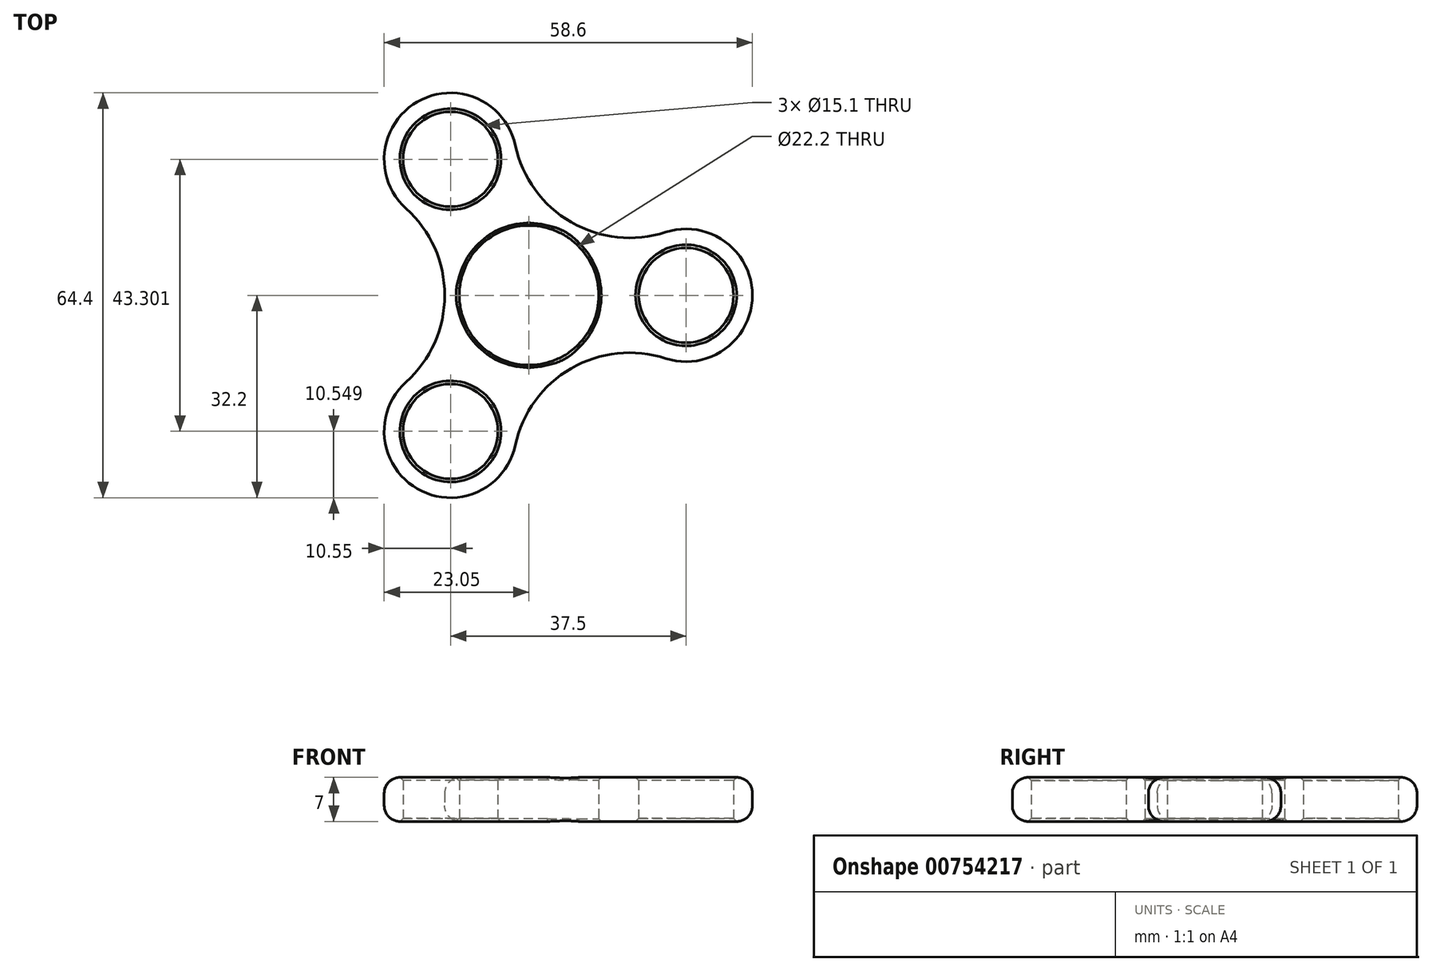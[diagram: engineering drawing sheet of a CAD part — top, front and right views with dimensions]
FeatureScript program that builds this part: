
annotation { "Feature Type Name" : "Feature", "Feature Type Description" : "" }
export const myFeature = defineFeature(function(context is Context, id is Id, definition is map)
    precondition{}
    {
        {
            var Q0;
            Q0=qCreatedBy(makeId("Top.planeOp"),FACE);
            var sketch = newSketch(context, id + "F0", { "sketchPlane" : qUnion([Q0])});
            skCircle(sketch, "E0", {"center": v(0, 0) * mm, "radius": 11.1 * mm});
            skPoint(sketch, "E1", {"position": v(25, 0) * mm});
            skCircle(sketch, "E2", {"center": v(25, 0) * mm, "radius": 7.55 * mm});
            skArc(sketch, "E3.0", {"start": v(21.75, -10.04) * mm, "mid": v(35.55, 0) * mm, "end": v(21.75, 10.04) * mm});
            skArc(sketch, "E4.1.0", {"start": v(-2.18, 23.85) * mm, "mid": v(-17.77, 30.79) * mm, "end": v(-19.57, 13.82) * mm});
            skCircle(sketch, "E4.1.1", {"center": v(-12.5, 21.65) * mm, "radius": 7.55 * mm});
            skArc(sketch, "E4.2.0", {"start": v(-19.57, -13.82) * mm, "mid": v(-17.78, -30.79) * mm, "end": v(-2.18, -23.85) * mm});
            skCircle(sketch, "E4.2.1", {"center": v(-12.5, -21.65) * mm, "radius": 7.55 * mm});
            skArc(sketch, "E5", {"start": v(-2.18, 23.85) * mm, "mid": v(6.71, 11.62) * mm, "end": v(21.75, 10.04) * mm});
            skArc(sketch, "E6", {"start": v(21.75, -10.04) * mm, "mid": v(6.71, -11.62) * mm, "end": v(-2.18, -23.85) * mm});
            skArc(sketch, "E7", {"start": v(-19.57, -13.82) * mm, "mid": v(-13.42, 0) * mm, "end": v(-19.57, 13.82) * mm});
            skSolve(sketch);
        }
        {
            var Q0;
            Q0=makeQuery(id+"F0.imprint","IMPRINT",FACE,{"disambiguationData":[TD([[makeQuery(id+"F0.imprint","IMPRINT",EDGE,{"derivedFrom":sQuery(id+"F0.wireOp",EDGE,"E4.1.1")}),-1.0]])]});
            var Q1;
            {var subQ0=sQuery(id+"F0.wireOp",EDGE,"E7");var subQ1=sQuery(id+"F0.wireOp",EDGE,"e07e0217-3c4f-4238-9027-1b7dd3b318d3.0");var subQ2=makeQuery(id+"F0.imprint","INTERSECT",VERTEX,{"derivedFrom":[subQ1,subQ0]});Q1=makeQuery(id+"F0.imprint","IMPRINT",FACE,{"disambiguationData":[TD([[makeQuery(id+"F0.imprint","IMPRINT",EDGE,{"disambiguationData":[TD([[subQ2,1.0]])],"derivedFrom":subQ1}),-1.0]])]});}
            var Q2;
            Q2=makeQuery(id+"F0.imprint","IMPRINT",FACE,{"disambiguationData":[TD([[makeQuery(id+"F0.imprint","IMPRINT",EDGE,{"derivedFrom":sQuery(id+"F0.wireOp",EDGE,"E0")}),-1.0]])]});
            var Q3;
            {var subQ0=sQuery(id+"F0.wireOp",EDGE,"E7");var subQ1=sQuery(id+"F0.wireOp",EDGE,"e07e0217-3c4f-4238-9027-1b7dd3b318d3.0");var subQ2=makeQuery(id+"F0.imprint","INTERSECT",VERTEX,{"derivedFrom":[subQ1,subQ0]});Q3=makeQuery(id+"F0.imprint","IMPRINT",FACE,{"disambiguationData":[TD([[makeQuery(id+"F0.imprint","IMPRINT",EDGE,{"disambiguationData":[TD([[subQ2,-1.0]])],"derivedFrom":subQ1}),-1.0]])]});}
            var Q4;
            Q4=makeQuery(id+"F0.imprint","IMPRINT",FACE,{"disambiguationData":[TD([[makeQuery(id+"F0.imprint","IMPRINT",EDGE,{"derivedFrom":sQuery(id+"F0.wireOp",EDGE,"E2")}),-1.0]])]});
            var Q5;
            {var subQ0=sQuery(id+"F0.wireOp",EDGE,"E5");var subQ1=sQuery(id+"F0.wireOp",EDGE,"e07e0217-3c4f-4238-9027-1b7dd3b318d3.0");var subQ2=makeQuery(id+"F0.imprint","INTERSECT",VERTEX,{"derivedFrom":[subQ1,subQ0]});Q5=makeQuery(id+"F0.imprint","IMPRINT",FACE,{"disambiguationData":[TD([[makeQuery(id+"F0.imprint","IMPRINT",EDGE,{"disambiguationData":[TD([[subQ2,1.0]])],"derivedFrom":subQ1}),-1.0]])]});}
            var Q6;
            Q6=makeQuery(id+"F0.imprint","IMPRINT",FACE,{"disambiguationData":[TD([[makeQuery(id+"F0.imprint","IMPRINT",EDGE,{"derivedFrom":sQuery(id+"F0.wireOp",EDGE,"E4.2.1")}),-1.0]])]});
            extrude(context, id + "F1", {"entities" : qUnion([Q0, Q1, Q2, Q3, Q4, Q5, Q6]), "depth" : 7 * mm, "offsetDistance" : 25 * mm});
        }
        {
            var Q0;
            Q0=makeQuery(id+"F1.opExtrude","CAP_EDGE",EDGE,{"disambiguationData":[OSD([sQuery(id+"F0.wireOp",EDGE,"E6")])],"isStart":true});
            var Q1;
            Q1=makeQuery(id+"F1.opExtrude","CAP_EDGE",EDGE,{"disambiguationData":[OSD([sQuery(id+"F0.wireOp",EDGE,"E6")])],"isStart":false});
            fillet(context, id + "F2", {"entities" : qUnion([Q0, Q1]), "radius" : 2.5 * mm, "tangentPropagation" : true, "allowEdgeOverflow" : false});
        }
        {
            var Q0;
            Q0=makeQuery(id+"F1.opExtrude","CAP_EDGE",EDGE,{"disambiguationData":[OSD([sQuery(id+"F0.wireOp",EDGE,"E0")])],"isStart":false});
            var Q1;
            Q1=makeQuery(id+"F1.opExtrude","CAP_EDGE",EDGE,{"disambiguationData":[OSD([sQuery(id+"F0.wireOp",EDGE,"E0")])],"isStart":true});
            chamfer(context, id + "F3", {"entities" : qUnion([Q0, Q1]), "width" : 0.4 * mm, "tangentPropagation" : true});
        }
        {
            var Q0;
            Q0=makeQuery(id+"F1.opExtrude","CAP_EDGE",EDGE,{"disambiguationData":[OSD([sQuery(id+"F0.wireOp",EDGE,"E4.1.1")])],"isStart":false});
            var Q1;
            Q1=makeQuery(id+"F1.opExtrude","CAP_EDGE",EDGE,{"disambiguationData":[OSD([sQuery(id+"F0.wireOp",EDGE,"E4.1.1")])],"isStart":true});
            var Q2;
            Q2=makeQuery(id+"F1.opExtrude","CAP_EDGE",EDGE,{"disambiguationData":[OSD([sQuery(id+"F0.wireOp",EDGE,"E4.2.1")])],"isStart":true});
            var Q3;
            Q3=makeQuery(id+"F1.opExtrude","CAP_EDGE",EDGE,{"disambiguationData":[OSD([sQuery(id+"F0.wireOp",EDGE,"E4.2.1")])],"isStart":false});
            var Q4;
            Q4=makeQuery(id+"F1.opExtrude","CAP_EDGE",EDGE,{"disambiguationData":[OSD([sQuery(id+"F0.wireOp",EDGE,"E2")])],"isStart":true});
            var Q5;
            Q5=makeQuery(id+"F1.opExtrude","CAP_EDGE",EDGE,{"disambiguationData":[OSD([sQuery(id+"F0.wireOp",EDGE,"E2")])],"isStart":false});
            chamfer(context, id + "F4", {"entities" : qUnion([Q0, Q1, Q2, Q3, Q4, Q5]), "width" : 0.5 * mm, "tangentPropagation" : true});
        }
    });
